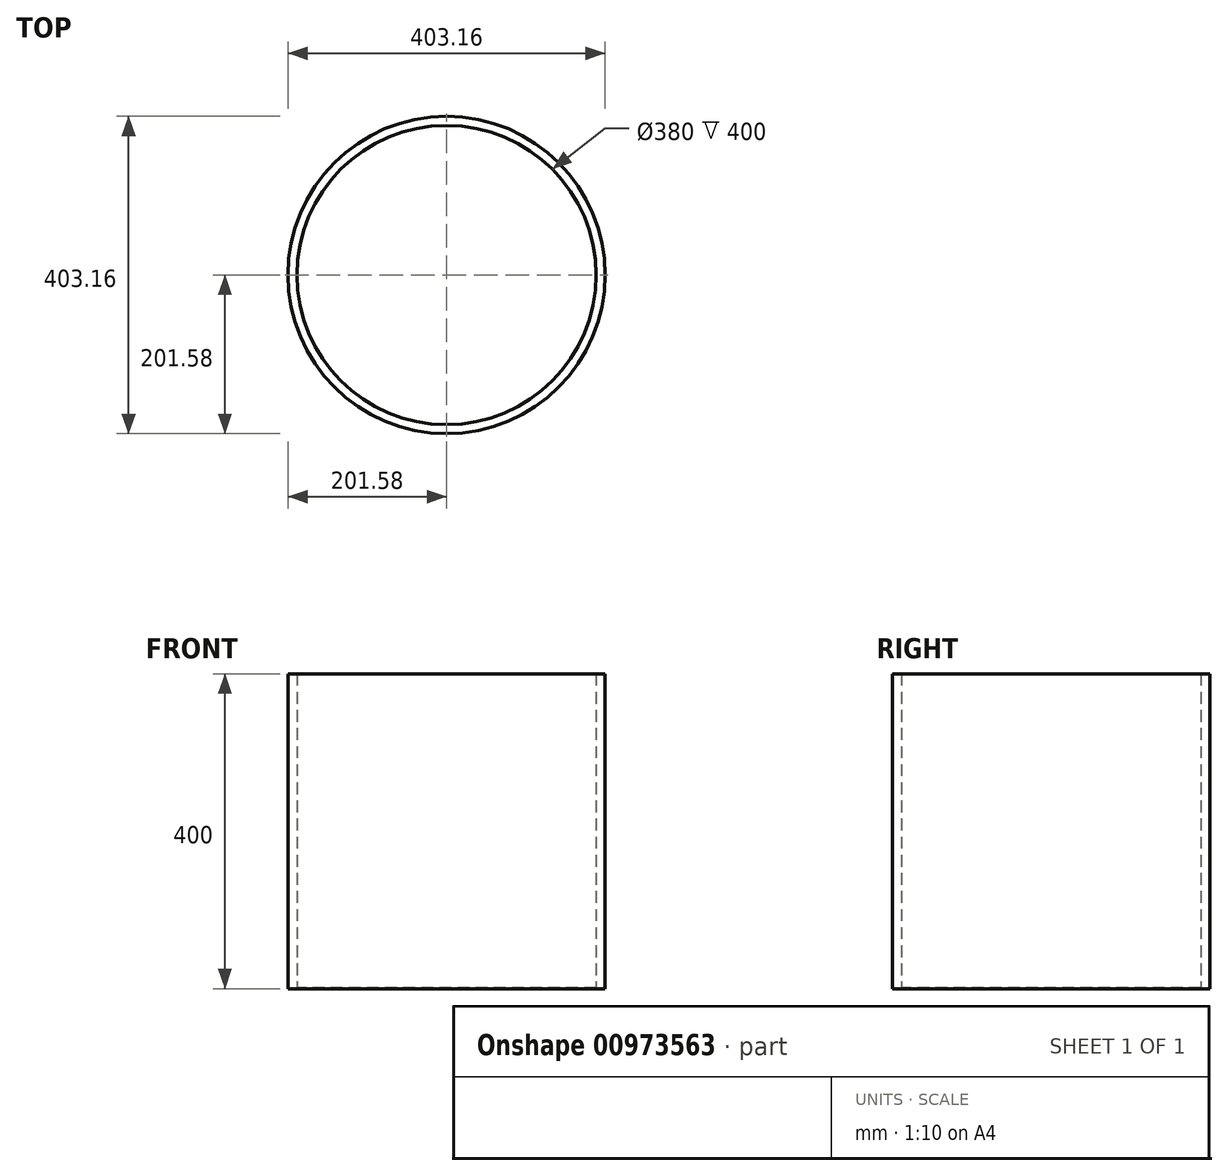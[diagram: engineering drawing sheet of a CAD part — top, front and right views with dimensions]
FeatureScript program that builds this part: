
annotation { "Feature Type Name" : "Feature", "Feature Type Description" : "" }
export const myFeature = defineFeature(function(context is Context, id is Id, definition is map)
    precondition{}
    {
        {
            var Q0;
            Q0=qCreatedBy(makeId("Top.planeOp"),FACE);
            var sketch = newSketch(context, id + "F0", { "sketchPlane" : qUnion([Q0])});
            skCircle(sketch, "E0", {"center": v(0, 0) * mm, "radius": 190 * mm});
            skCircle(sketch, "E1", {"center": v(0, 0) * mm, "radius": 201.58 * mm});
            skSolve(sketch);
        }
        {
            var Q0;
            Q0=makeQuery(id+"F0.imprint","IMPRINT",FACE,{"disambiguationData":[TD([[makeQuery(id+"F0.imprint","IMPRINT",EDGE,{"derivedFrom":sQuery(id+"F0.wireOp",EDGE,"E0")}),-1.0]])]});
            var Q1;
            Q1=sQuery(id+"F0.wireOp",EDGE,"E1");
            var Q2;
            Q2=sQuery(id+"F0.wireOp",EDGE,"E0");
            extrude(context, id + "F1", {"entities" : qUnion([Q0]), "surfaceEntities" : qUnion([Q1, Q2]), "depth" : 400 * mm, "offsetDistance" : 25 * mm});
        }
        {
            var Q0;
            Q0=makeQuery(id+"F0.imprint","IMPRINT",FACE,{"disambiguationData":[TD([[makeQuery(id+"F0.imprint","IMPRINT",EDGE,{"derivedFrom":sQuery(id+"F0.wireOp",EDGE,"E0")}),1.0]])]});
            var Q1;
            Q1=sQuery(id+"F0.wireOp",EDGE,"E0");
            extrude(context, id + "F2", {"entities" : qUnion([Q0]), "surfaceEntities" : qUnion([Q1]), "depth" : 1 * mm, "offsetDistance" : 25 * mm});
        }
    });
